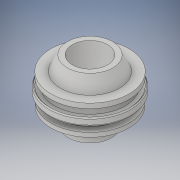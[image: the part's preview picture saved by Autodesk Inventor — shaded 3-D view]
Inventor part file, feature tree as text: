
AUTODESK INVENTOR PART (.ipt)
format: ipt  version: 2017 (Build 210142000, 142)  size: 181,760 bytes
history: native  units: in
note: dims shown in document units (in); Inventor stores cm internally (conversion verified against a paired STEP export)
features: revolve x1, sketch x1
ambient origin geometry x8: Origin, YZ Plane, XZ Plane, XY Plane, X Axis, Y Axis, Z Axis, Center Point
bodies: Solid1 (feature_tree)
feature tree (2):
  revolve  "Revolution1"  [1 undecoded]
  sketch  "Sketch1"  dims[d0=0.25in d3=8.0in d6=0.7902in d8=0.7902in d9=90.0deg d11=1.5in d12=1.5in d13=0.0in d14=1.0in d15=0.0in d16=0.7902in d17=0.7902in]
note: 1 required parameter value undecoded (feature->parameter linkage not recoverable at this tier; creation-order binding heuristic only, values carry confidence <= 0.55)
